# Revit family: Diffuser-Carnes-T_Bar_Mount-1-Slot-DHAB
name_source: partatom
category: Duct Accessories
revit_build: Autodesk Revit MEP 2014 (Build: 20130308_1515(x64)
units: mm (PartAtom-declared; Revit-internal decimal feet)

## types (36) — shared parameters
B Radius = 63"
Catalog = http://www.carnes.com
D Depth = 2 3/4"
Default Elevation = 0"
Depth = 2 3/4"
Description = Extruded Aluminum 1 Slot Diffuser 15/16In T-Bar Tegular Mount
Flow = 0 CFM
Height = 9 1/16"
Inlet Width = 60"
Manufacturer = CARNES COMPANY
Model = DHAB
Product Page URL = http://www.carnes.com
Profile Depth = 5 193/256"
Revit Object Download Link = http://library.smartbim.com
Specification Sheet = http://www.carnes.com
Subcatagory = Air Distribution
Supply Connection = Diffuser Supply Connector
Supply Connector = Yes
URL = http://www.carnes.com
Unit = Metal - Carnes - Steel Galvanized

## per-type parameters (varying)
| type | Box Length | Inlet Nominal Size Height D | Inlet Nominal Size Width | Inlet Offset | Length |
| DHAB 24 x 5In | 23 1/2" | 3 1/2" | 5" | 10 1/2" | 24" |
| DHAB 24 x 6IN | 23 1/2" | 3 1/2" | 6" | 10 1/2" | 24" |
| DHAB 24 x 7IN | 23 1/2" | 5 1/4" | 7" | 10 1/2" | 24" |
| DHAB 24 x 8IN | 23 1/2" | 5 1/4" | 8" | 10 1/2" | 24" |
| DHAB 24 x 10IN | 23 1/2" | 5 1/4" | 10" | 10 1/2" | 24" |
| DHAB 24 x 12IN | 23 1/2" | 5 1/4" | 12" | 10 1/2" | 24" |
| DHAB 30 x 5In | 29 1/2" | 3 1/2" | 5" | 14 1/2" | 30" |
| DHAB 30 x 6IN | 29 1/2" | 3 1/2" | 6" | 14 1/2" | 30" |
| DHAB 30 x 7IN | 29 1/2" | 5 1/4" | 7" | 14 1/2" | 30" |
| DHAB 30 x 8IN | 29 1/2" | 5 1/4" | 8" | 14 1/2" | 30" |
| DHAB 30 x 10IN | 29 1/2" | 5 1/4" | 10" | 14 1/2" | 30" |
| DHAB 30 x 12IN | 29 1/2" | 5 1/4" | 12" | 14 1/2" | 30" |
| DHAB 36 x 5In | 35 1/2" | 3 1/2" | 5" | 17 1/2" | 36" |
| DHAB 36 x 6IN | 35 1/2" | 3 1/2" | 6" | 17 1/2" | 36" |
| DHAB 36 x 7IN | 35 1/2" | 5 1/4" | 7" | 17 1/2" | 36" |
| DHAB 36 x 8IN | 35 1/2" | 5 1/4" | 8" | 17 1/2" | 36" |
| DHAB 36 x 10IN | 35 1/2" | 5 1/4" | 10" | 17 1/2" | 36" |
| DHAB 36 x 12IN | 35 1/2" | 5 1/4" | 12" | 17 1/2" | 36" |
| DHAB 48 x 5In | 47 1/2" | 3 1/2" | 5" | 23 1/2" | 48" |
| DHAB 48 x 6IN | 47 1/2" | 3 1/2" | 6" | 23 1/2" | 48" |
| DHAB 48 x 7IN | 47 1/2" | 5 1/4" | 7" | 23 1/2" | 48" |
| DHAB 48 x 8IN | 47 1/2" | 5 1/4" | 8" | 23 1/2" | 48" |
| DHAB 48 x 10IN | 47 1/2" | 5 1/4" | 10" | 23 1/2" | 48" |
| DHAB 48 x 12IN | 47 1/2" | 5 1/4" | 12" | 23 1/2" | 48" |
| DHAB 60 x 5In | 59 1/2" | 3 1/2" | 5" | 29 1/2" | 60" |
| DHAB 60 x 6IN | 59 1/2" | 3 1/2" | 6" | 29 1/2" | 60" |
| DHAB 60 x 7IN | 59 1/2" | 5 1/4" | 7" | 29 1/2" | 60" |
| DHAB 60 x 8IN | 59 1/2" | 5 1/4" | 8" | 29 1/2" | 60" |
| DHAB 60 x 10IN | 59 1/2" | 5 1/4" | 10" | 29 1/2" | 60" |
| DHAB 60 x 12IN | 59 1/2" | 5 1/4" | 12" | 29 1/2" | 60" |
| DHAB 72 x 5In | 71 1/2" | 3 1/2" | 5" | 35 1/2" | 72" |
| DHAB 72 x 6IN | 71 1/2" | 3 1/2" | 6" | 35 1/2" | 72" |
| DHAB 72 x 7IN | 71 1/2" | 5 1/4" | 7" | 35 1/2" | 72" |
| DHAB 72 x 8IN | 71 1/2" | 5 1/4" | 8" | 35 1/2" | 72" |
| DHAB 72 x 10IN | 71 1/2" | 5 1/4" | 10" | 35 1/2" | 72" |
| DHAB 72 x 12IN | 71 1/2" | 5 1/4" | 12" | 35 1/2" | 72" |

## geometry (parser evidence)
native form markers: Blend x2, Sweep x9
no freeform markers — native parametric forms only
